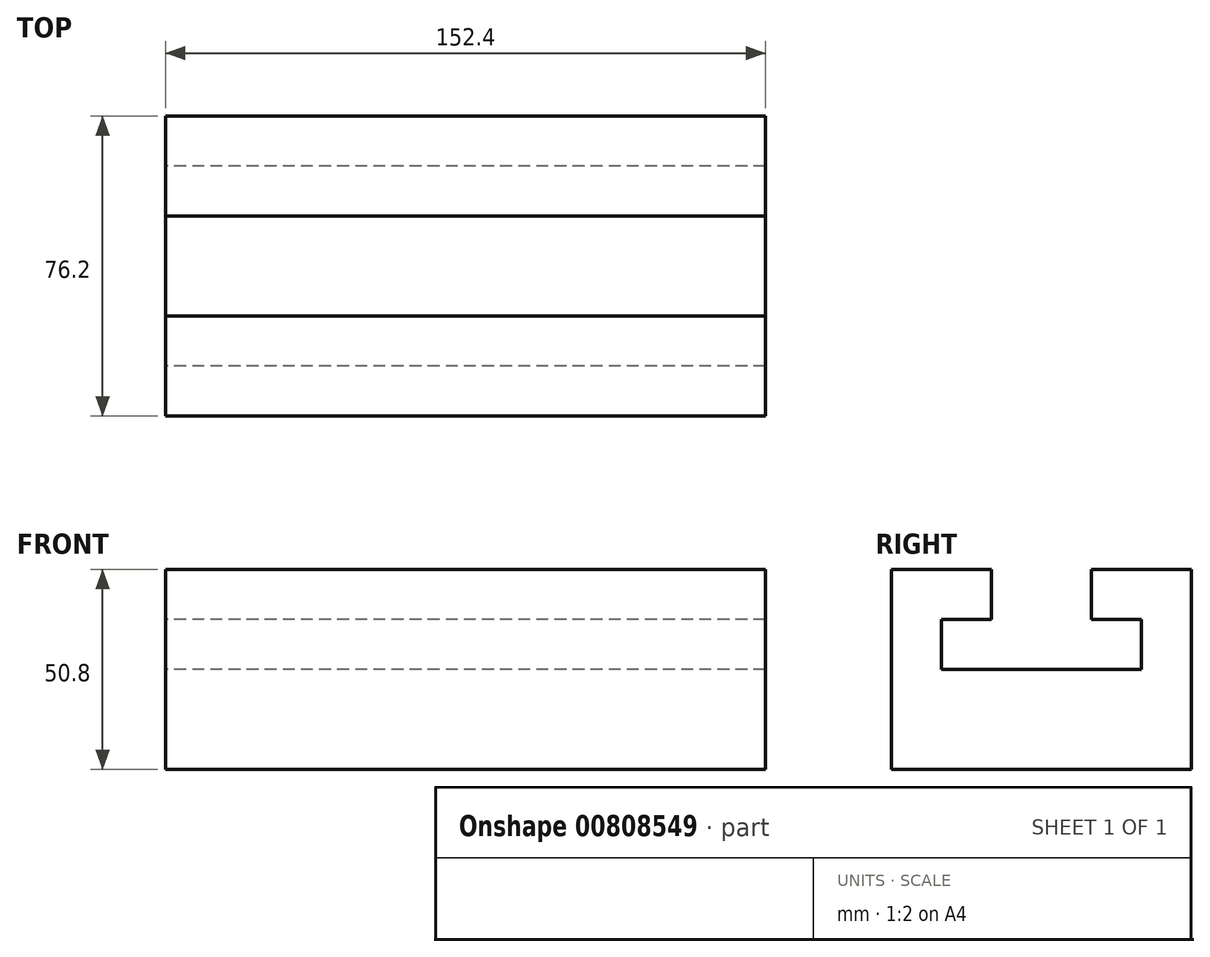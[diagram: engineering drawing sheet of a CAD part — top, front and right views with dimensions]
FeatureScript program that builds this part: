
annotation { "Feature Type Name" : "Feature", "Feature Type Description" : "" }
export const myFeature = defineFeature(function(context is Context, id is Id, definition is map)
    precondition{}
    {
        {
            var Q0;
            Q0=qCreatedBy(makeId("Right.planeOp"),FACE);
            var sketch = newSketch(context, id + "F0", { "sketchPlane" : qUnion([Q0])});
            skLineSegment(sketch, "E0", {"start": v(-35.49, 21.8) * mm, "end": v(-35.49, -29) * mm});
            skLineSegment(sketch, "E1", {"start": v(-35.49, -29) * mm, "end": v(40.71, -29) * mm});
            skLineSegment(sketch, "E2", {"start": v(40.71, -29) * mm, "end": v(40.71, 21.8) * mm});
            skLineSegment(sketch, "E3", {"start": v(40.71, 21.8) * mm, "end": v(15.31, 21.8) * mm});
            skLineSegment(sketch, "E4", {"start": v(15.31, 21.8) * mm, "end": v(15.31, 9.1) * mm});
            skLineSegment(sketch, "E5", {"start": v(15.31, 9.1) * mm, "end": v(28.01, 9.1) * mm});
            skLineSegment(sketch, "E6", {"start": v(28.01, 9.1) * mm, "end": v(28.01, -3.6) * mm});
            skLineSegment(sketch, "E7", {"start": v(28.01, -3.6) * mm, "end": v(-22.79, -3.6) * mm});
            skLineSegment(sketch, "E8", {"start": v(-22.79, -3.6) * mm, "end": v(-22.79, 9.1) * mm});
            skLineSegment(sketch, "E9", {"start": v(-22.79, 9.1) * mm, "end": v(-10.09, 9.1) * mm});
            skLineSegment(sketch, "E10", {"start": v(-10.09, 9.1) * mm, "end": v(-10.09, 21.8) * mm});
            skLineSegment(sketch, "E11", {"start": v(-10.09, 21.8) * mm, "end": v(-35.49, 21.8) * mm});
            skSolve(sketch);
        }
        {
            var Q0;
            Q0=makeQuery(id+"F0.imprint","IMPRINT",FACE,{"disambiguationData":[TD([[makeQuery(id+"F0.imprint","IMPRINT",EDGE,{"derivedFrom":sQuery(id+"F0.wireOp",EDGE,"E0")}),1.0]])]});
            extrude(context, id + "F1", {"entities" : qUnion([Q0]), "depth" : 152.4 * mm, "offsetDistance" : 25.4 * mm});
        }
    });
